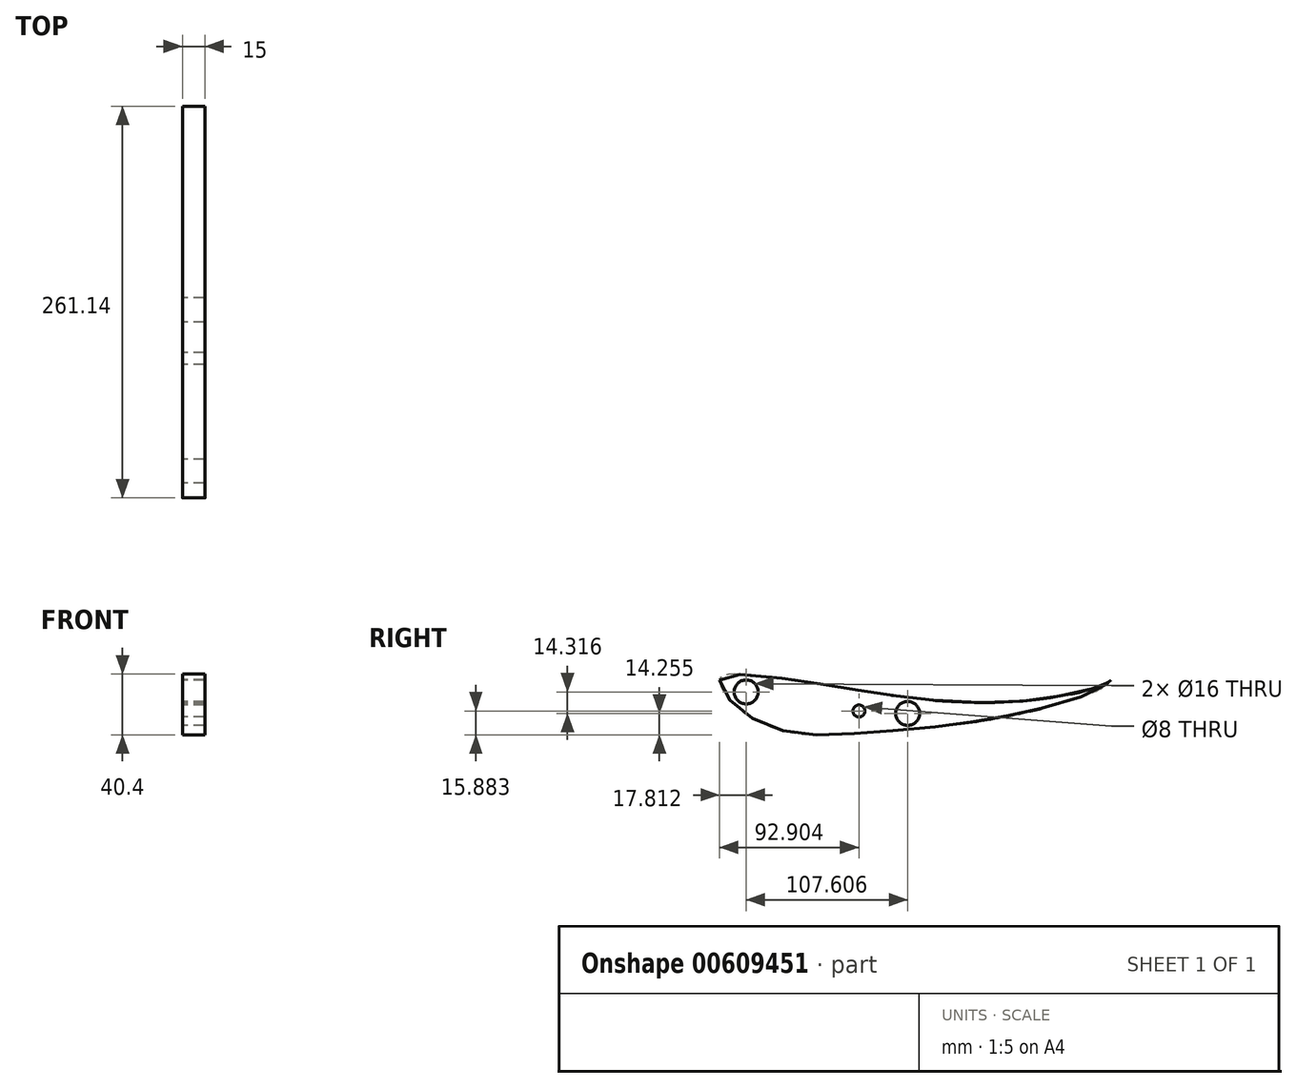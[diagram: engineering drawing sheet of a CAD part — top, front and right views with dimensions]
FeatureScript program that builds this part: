
annotation { "Feature Type Name" : "Feature", "Feature Type Description" : "" }
export const myFeature = defineFeature(function(context is Context, id is Id, definition is map)
    precondition{}
    {
        {
            var Q0;
            Q0=qCreatedBy(makeId("Right.planeOp"),FACE);
            var sketch = newSketch(context, id + "F0", { "sketchPlane" : qUnion([Q0])});
            skFitSpline(sketch, "E0", {"points": [v(-82.9, 15.31) * mm, v(-82.72, 13.45) * mm, v(-81.93, 10.89) * mm, v(-80.76, 8.46) * mm, v(-78.77, 5.4) * mm, v(-76.46, 2.43) * mm, v(-74.09, 0.05) * mm, v(-71.02, -2.74) * mm, v(-66.36, -6.45) * mm, v(-62.04, -9.39) * mm, v(-56.67, -12.3) * mm, v(-51.53, -14.76) * mm, v(-44.09, -17.33) * mm, v(-39.83, -18.56) * mm, v(-32.87, -19.86) * mm, v(-27.68, -20.5) * mm, v(-20.48, -21.04) * mm, v(-10.15, -21.04) * mm, v(-4.84, -20.82) * mm, v(2.75, -20.53) * mm, v(12.43, -19.83) * mm, v(19.42, -19.31) * mm, v(27.83, -18.65) * mm, v(39.73, -17.7) * mm, v(49.58, -16.82) * mm, v(59.18, -15.88) * mm, v(70.48, -14.64) * mm, v(77.85, -13.71) * mm, v(85.2, -12.7) * mm, v(92.53, -11.55) * mm, v(97.88, -10.6) * mm, v(104.42, -9.42) * mm, v(110.6, -8.26) * mm, v(116.81, -6.9) * mm, v(123.02, -5.5) * mm, v(131.68, -3.53) * mm, v(138.5, -1.66) * mm, v(148.52, 1.07) * mm, v(159.76, 4.77) * mm, v(166.04, 7.2) * mm, v(170, 9.1) * mm, v(173.56, 11.24) * mm, v(176.2, 13.38) * mm, v(178.2, 15.16) * mm, v(175.24, 13.46) * mm, v(172.23, 12.09) * mm, v(167.34, 10.21) * mm, v(162.56, 8.66) * mm, v(157.84, 7.47) * mm, v(151.53, 6.06) * mm, v(144.02, 4.71) * mm, v(136.8, 3.42) * mm, v(129.62, 2.55) * mm, v(120.29, 1.49) * mm, v(113.26, 1.09) * mm, v(103.2, 0.48) * mm, v(89.6, 0.4) * mm, v(72.19, 0.9) * mm, v(62.19, 1.65) * mm, v(56.7, 2.08) * mm, v(49.82, 2.85) * mm, v(42.61, 3.72) * mm, v(30.76, 5.31) * mm, v(22.33, 6.5) * mm, v(15.3, 7.74) * mm, v(6.4, 9.02) * mm, v(-0.72, 10.25) * mm, v(-8.45, 11.51) * mm, v(-18.15, 13.11) * mm, v(-26.18, 14.43) * mm, v(-35.39, 15.88) * mm, v(-43.7, 16.98) * mm, v(-53.58, 18.04) * mm, v(-64.74, 18.86) * mm, v(-72.87, 19.27) * mm, v(-77.52, 18.92) * mm, v(-79.16, 18.77) * mm, v(-80.9, 18.34) * mm, v(-81.94, 17.48) * mm, v(-82.9, 15.31) * mm]});
            skPoint(sketch, "E1", {"position": v(-65.13, 7.45) * mm});
            skCircle(sketch, "E2", {"center": v(-65.13, 7.45) * mm, "radius": 8 * mm});
            skPoint(sketch, "E3", {"position": v(42.48, -6.86) * mm});
            skCircle(sketch, "E4", {"center": v(42.48, -6.86) * mm, "radius": 8 * mm});
            skPoint(sketch, "E5", {"position": v(9.96, -5.24) * mm});
            skCircle(sketch, "E6", {"center": v(9.96, -5.24) * mm, "radius": 4 * mm});
            skSolve(sketch);
        }
        {
            var Q0;
            Q0=makeQuery(id+"F0.imprint","IMPRINT",FACE,{"disambiguationData":[TD([[makeQuery(id+"F0.imprint","IMPRINT",EDGE,{"derivedFrom":sQuery(id+"F0.wireOp",EDGE,"E0")}),1.0]])]});
            extrude(context, id + "F1", {"entities" : qUnion([Q0]), "depth" : 15 * mm, "offsetDistance" : 25.4 * mm});
        }
    });
